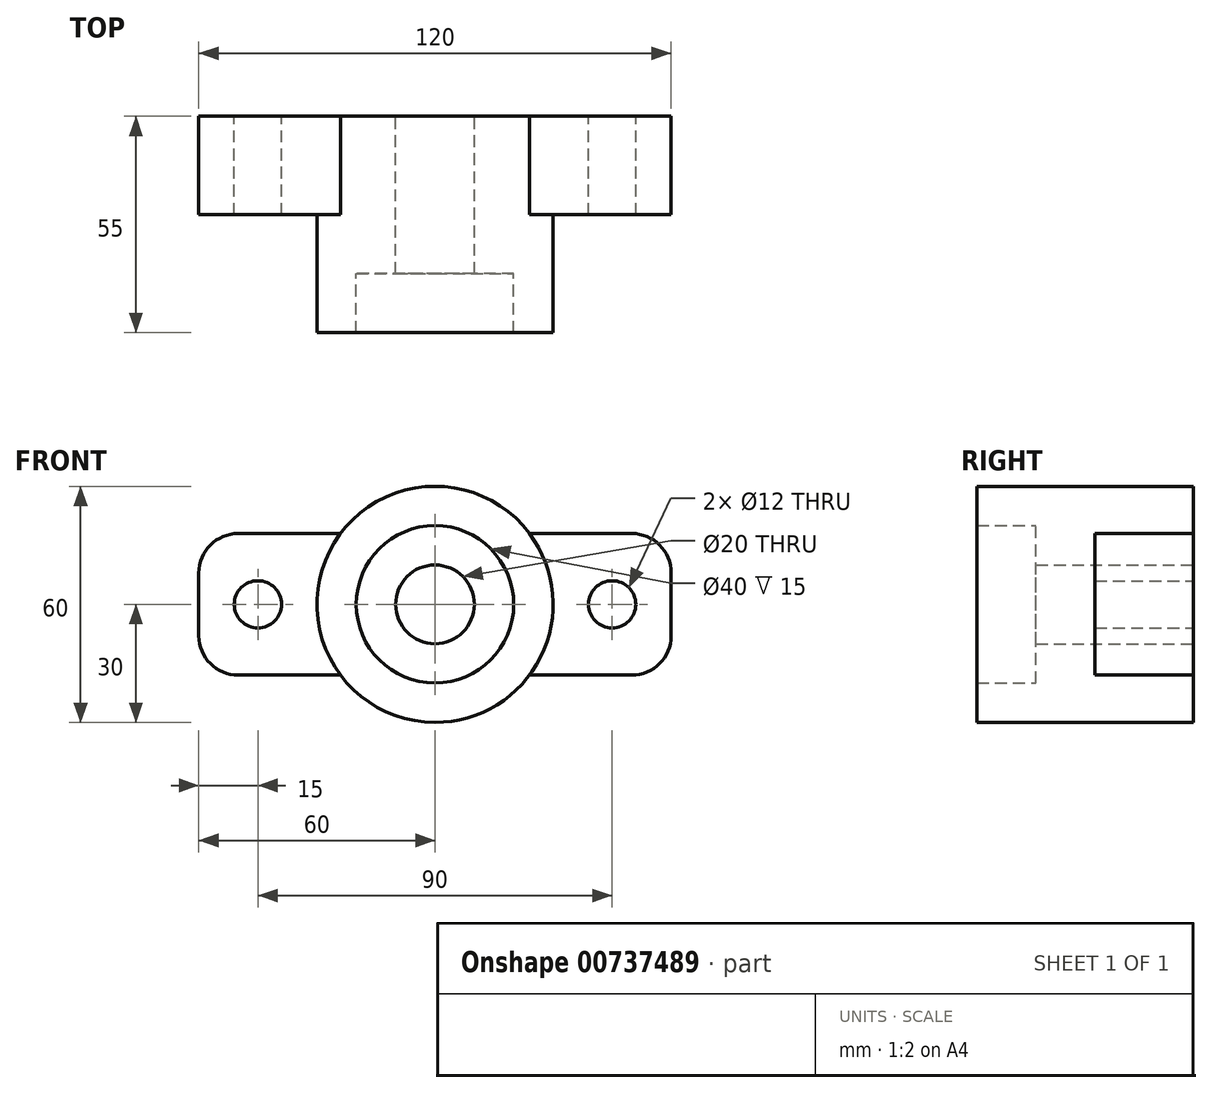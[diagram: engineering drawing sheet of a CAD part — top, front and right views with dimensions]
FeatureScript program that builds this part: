
annotation { "Feature Type Name" : "Feature", "Feature Type Description" : "" }
export const myFeature = defineFeature(function(context is Context, id is Id, definition is map)
    precondition{}
    {
        {
            var Q0;
            Q0=qCreatedBy(makeId("Front.planeOp"),FACE);
            var sketch = newSketch(context, id + "F0", { "sketchPlane" : qUnion([Q0])});
            skCircle(sketch, "E0", {"center": v(0, 0) * mm, "radius": 30 * mm});
            skLineSegment(sketch, "E1.bottom", {"start": v(50, 18) * mm, "end": v(-50, 18) * mm});
            skLineSegment(sketch, "E1.top", {"start": v(60, -18) * mm, "end": v(-60, -18) * mm});
            skLineSegment(sketch, "E1.left", {"start": v(60, 8) * mm, "end": v(60, -8) * mm});
            skLineSegment(sketch, "E1.right", {"start": v(-60, 8) * mm, "end": v(-60, -8) * mm});
            skLineSegment(sketch, "E2", {"start": v(-50, -18) * mm, "end": v(-45, -18) * mm});
            skLineSegment(sketch, "E3", {"start": v(50, -18) * mm, "end": v(45, -18) * mm});
            skLineSegment(sketch, "E4", {"start": v(-45, -18) * mm, "end": v(-45, 0) * mm});
            skLineSegment(sketch, "E5", {"start": v(45, -18) * mm, "end": v(45, 0) * mm});
            skCircle(sketch, "E6", {"center": v(-45, 0) * mm, "radius": 6 * mm});
            skCircle(sketch, "E7", {"center": v(45, 0) * mm, "radius": 6 * mm});
            skPoint(sketch, "E8.visualSharp", {"position": v(-60, 18) * mm});
            skArc(sketch, "E8.filletArc", {"start": v(-50, 18) * mm, "mid": v(-57.07, 15.07) * mm, "end": v(-60, 8) * mm});
            skPoint(sketch, "E9.visualSharp", {"position": v(60, 18) * mm});
            skArc(sketch, "E9.filletArc", {"start": v(60, 8) * mm, "mid": v(57.07, 15.07) * mm, "end": v(50, 18) * mm});
            skPoint(sketch, "E10.visualSharp", {"position": v(-60, -18) * mm});
            skArc(sketch, "E10.filletArc", {"start": v(-60, -8) * mm, "mid": v(-57.07, -15.07) * mm, "end": v(-50, -18) * mm});
            skPoint(sketch, "E11.visualSharp", {"position": v(60, -18) * mm});
            skArc(sketch, "E11.filletArc", {"start": v(50, -18) * mm, "mid": v(57.07, -15.07) * mm, "end": v(60, -8) * mm});
            skCircle(sketch, "E12", {"center": v(0, 0) * mm, "radius": 10 * mm});
            skSolve(sketch);
        }
        {
            var Q0;
            Q0 = qSketchRegion(id + "F0", true);
            extrude(context, id + "F1", {"entities" : qUnion([Q0]), "depth" : 25 * mm, "offsetDistance" : 25 * mm});
        }
        {
            var Q0;
            Q0=makeQuery(id+"F1.opExtrude","CAP_FACE",FACE,{"disambiguationData":[OSD([sQuery(id+"F0.wireOp",EDGE,"E0"),sQuery(id+"F0.wireOp",EDGE,"E1.bottom"),sQuery(id+"F0.wireOp",EDGE,"E1.top"),sQuery(id+"F0.wireOp",EDGE,"E1.left"),sQuery(id+"F0.wireOp",EDGE,"E1.right"),sQuery(id+"F0.wireOp",EDGE,"E2"),sQuery(id+"F0.wireOp",EDGE,"E3"),sQuery(id+"F0.wireOp",EDGE,"E6"),sQuery(id+"F0.wireOp",EDGE,"E7"),sQuery(id+"F0.wireOp",EDGE,"E8.filletArc"),sQuery(id+"F0.wireOp",EDGE,"E9.filletArc"),sQuery(id+"F0.wireOp",EDGE,"E10.filletArc"),sQuery(id+"F0.wireOp",EDGE,"E11.filletArc"),sQuery(id+"F0.wireOp",EDGE,"E12")])],"isStart":false});
            var sketch = newSketch(context, id + "F2", { "sketchPlane" : qUnion([Q0])});
            skCircle(sketch, "E13", {"center": v(0, 0) * mm, "radius": 30 * mm});
            skCircle(sketch, "E14", {"center": v(0, 0) * mm, "radius": 10 * mm});
            skSolve(sketch);
        }
        {
            var Q0;
            Q0 = qSketchRegion(id + "F2", true);
            extrude(context, id + "F3", {"entities" : qUnion([Q0]), "operationType" : NewBodyOperationType.ADD, "depth" : 15 * mm, "offsetDistance" : 25 * mm});
        }
        {
            var Q0;
            Q0=makeQuery(id+"F3.opExtrude","CAP_FACE",FACE,{"disambiguationData":[OSD([sQuery(id+"F2.wireOp",EDGE,"E13"),sQuery(id+"F2.wireOp",EDGE,"E14")])],"isStart":false});
            var sketch = newSketch(context, id + "F4", { "sketchPlane" : qUnion([Q0])});
            skCircle(sketch, "E15", {"center": v(0, 0) * mm, "radius": 30 * mm});
            skCircle(sketch, "E16", {"center": v(0, 0) * mm, "radius": 20 * mm});
            skSolve(sketch);
        }
        {
            var Q0;
            Q0=makeQuery(id+"F4.imprint","IMPRINT",FACE,{"disambiguationData":[TD([[makeQuery(id+"F4.imprint","IMPRINT",EDGE,{"derivedFrom":sQuery(id+"F4.wireOp",EDGE,"E15")}),1.0]])]});
            extrude(context, id + "F5", {"entities" : qUnion([Q0]), "operationType" : NewBodyOperationType.ADD, "depth" : 15 * mm, "offsetDistance" : 25 * mm});
        }
    });
